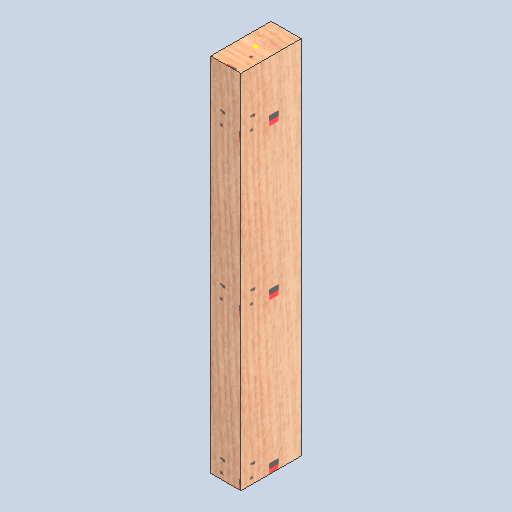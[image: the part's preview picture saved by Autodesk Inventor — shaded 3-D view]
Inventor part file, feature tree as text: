
AUTODESK INVENTOR PART (.ipt)
format: ipt  version: 2025 (Build 290162000, 162)  size: 184,832 bytes
history: native  units: in
note: dims shown in document units (in); Inventor stores cm internally (conversion verified against a paired STEP export)
features: sketch x2, extrude x1
ambient origin geometry x8: Origin, YZ Plane, XZ Plane, XY Plane, X Axis, Y Axis, Z Axis, Center Point
bodies: Solid1 (feature_tree)
feature tree (3):
  extrude  "Extrusion1"  Depth=4.0in
  sketch  "Sketch2"  dims[d2=24.0in d3=0.0in]
  sketch  "Sketch1"  dims[d0=2.0in d1=4.0in]
